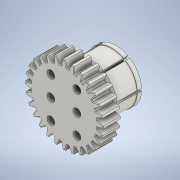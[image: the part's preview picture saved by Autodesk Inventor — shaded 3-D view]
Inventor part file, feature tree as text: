
AUTODESK INVENTOR PART (.ipt)
format: ipt  version: 2022 (Build 260153000, 153)  size: 884,736 bytes
history: native  units: mm (DEFAULTED — no unit token found)
features: sketch x8, extrude x6, plane x3, other x3, fillet x3, pattern_circular x2, revolve x1
ambient origin geometry x8: Origin, YZ Plane, XZ Plane, XY Plane, X Axis, Y Axis, Z Axis, Center Point
bodies: Solid1 (feature_tree)
feature tree (26):
  extrude  "Extrusion1"  Depth=10.0mm TaperAngle=0.0deg
  plane  "Work Plane2"
  plane  "Work Plane8"
  plane  "Work Plane9"
  other  "Цилиндрическое зубчатое зацепление"
  fillet  "Сопряжение1"  Radius=42.0mm
  pattern_circular  "Круговой массив1"  [2 undecoded]
  extrude  "Выдавливание5"  Depth=0.3mm TaperAngle=0.0deg
  extrude  "Выдавливание6"  TaperAngle=0.0deg  [1 undecoded]
  extrude  "Выдавливание7"  TaperAngle=0.0deg  [1 undecoded]
  revolve  "Вращение1"
  extrude  "Выдавливание8"  Depth=0.3mm
  extrude  "Выдавливание9"  Depth=0.3mm
  fillet  "Сопряжение3"  [1 undecoded]
  pattern_circular  "Круговой массив2"  [2 undecoded]
  fillet  "Сопряжение4"  Radius=280.0mm
  sketch  "Sketch1"  dims[d0=45.1mm d1=10.0mm d2=0.0mm d3=42.0mm]
  sketch  "Sketch2"  dims[d4=10.0mm d5=0.0mm d16=41.3mm d17=0.0mm d34=1.121997mm d39=0.0mm d41=0.0mm d43=41.3mm d46=41.3mm d47=0.0mm d48=0.0mm d49=0.4mm d50=280.0mm d51=360.0deg d75=15.0mm d76=23.0mm d77=4.5mm d78=20.0mm d80=15.0mm d81=30.0mm d83=11.5mm d86=10.0mm d87=0.0mm d88=2.0mm d89=0.0mm d90=25.4mm d91=2.0mm d92=0.436332mm d93=0.436332mm d94=60.0mm d96=360.0deg d98=20.0mm d99=0.0mm d100=0.3mm d101=12.0mm d102=2.5mm d103=90.0deg d104=21.0mm d105=20.0mm d106=0.0mm d107=0.872665mm d108=0.3mm d109=10.0mm d110=0.0mm d111=0.3mm d112=80.0mm d113=360.0deg d115=0.3mm]
  other  "Srf1"
  sketch  "Эскиз6"
  sketch  "Эскиз7"
  sketch  "Эскиз8"
  sketch  "Эскиз9"
  sketch  "Эскиз10"
  sketch  "Эскиз11"
  other  "Средний диаметр"
note: 7 required parameter values undecoded (feature->parameter linkage not recoverable at this tier; creation-order binding heuristic only, values carry confidence <= 0.55)
